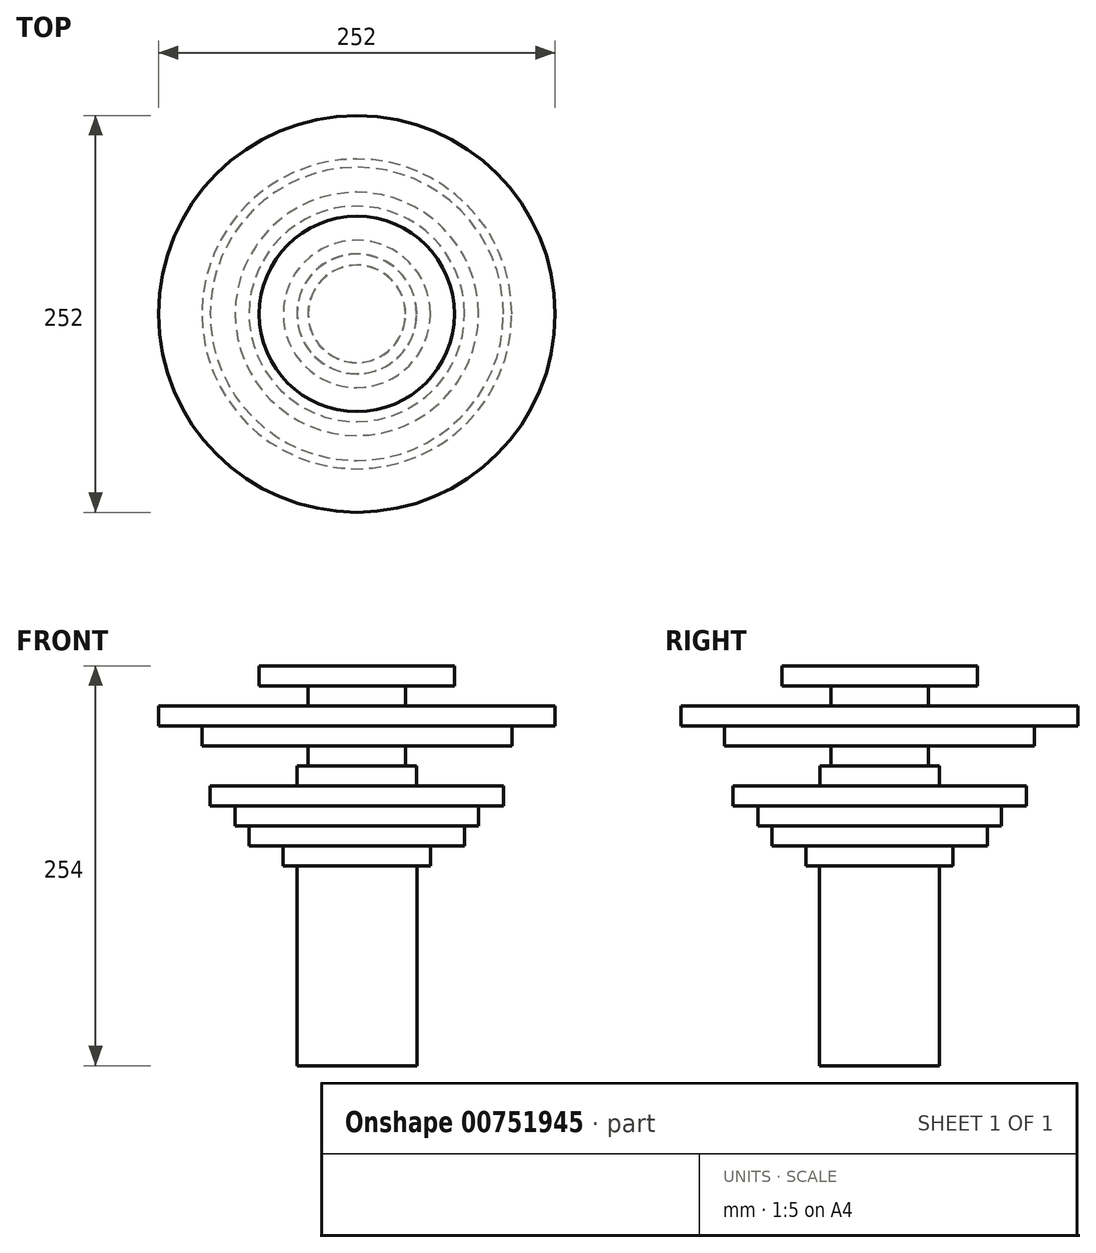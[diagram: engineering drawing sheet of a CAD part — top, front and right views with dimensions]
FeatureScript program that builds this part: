
annotation { "Feature Type Name" : "Feature", "Feature Type Description" : "" }
export const myFeature = defineFeature(function(context is Context, id is Id, definition is map)
    precondition{}
    {
        {
            var Q0;
            Q0=qCreatedBy(makeId("Front.planeOp"),FACE);
            var sketch = newSketch(context, id + "F0", { "sketchPlane" : qUnion([Q0])});
            skLineSegment(sketch, "E0.bottom", {"start": v(0, 10.4) * mm, "end": v(62, 10.4) * mm});
            skLineSegment(sketch, "E0.top", {"start": v(0, -2.3) * mm, "end": v(62, -2.3) * mm});
            skLineSegment(sketch, "E0.left", {"start": v(0, 10.4) * mm, "end": v(0, -2.3) * mm});
            skLineSegment(sketch, "E0.right", {"start": v(62, 10.4) * mm, "end": v(62, -2.3) * mm});
            skPoint(sketch, "E1.oppositeSnap0", {"position": v(31, -2.3) * mm});
            skLineSegment(sketch, "E1.bottom", {"start": v(0, -2.3) * mm, "end": v(31, -2.3) * mm});
            skLineSegment(sketch, "E1.top", {"start": v(0, -15) * mm, "end": v(31, -15) * mm});
            skLineSegment(sketch, "E1.left", {"start": v(0, -2.3) * mm, "end": v(0, -15) * mm});
            skLineSegment(sketch, "E1.right", {"start": v(31, -2.3) * mm, "end": v(31, -15) * mm});
            skLineSegment(sketch, "E2.bottom", {"start": v(0, -15) * mm, "end": v(126, -15) * mm});
            skLineSegment(sketch, "E2.top", {"start": v(0, -27.7) * mm, "end": v(126, -27.7) * mm});
            skLineSegment(sketch, "E2.left", {"start": v(0, -15) * mm, "end": v(0, -27.7) * mm});
            skLineSegment(sketch, "E2.right", {"start": v(126, -15) * mm, "end": v(126, -27.7) * mm});
            skLineSegment(sketch, "E3.bottom", {"start": v(0, -27.7) * mm, "end": v(98.4, -27.7) * mm});
            skLineSegment(sketch, "E3.top", {"start": v(0, -40.4) * mm, "end": v(98.4, -40.4) * mm});
            skLineSegment(sketch, "E3.left", {"start": v(0, -27.7) * mm, "end": v(0, -40.4) * mm});
            skLineSegment(sketch, "E3.right", {"start": v(98.4, -27.7) * mm, "end": v(98.4, -40.4) * mm});
            skLineSegment(sketch, "E4.bottom", {"start": v(0, -40.4) * mm, "end": v(30.9, -40.4) * mm});
            skLineSegment(sketch, "E4.top", {"start": v(0, -53.1) * mm, "end": v(30.9, -53.1) * mm});
            skLineSegment(sketch, "E4.left", {"start": v(0, -40.4) * mm, "end": v(0, -53.1) * mm});
            skLineSegment(sketch, "E4.right", {"start": v(30.9, -40.4) * mm, "end": v(30.9, -53.1) * mm});
            skLineSegment(sketch, "E5.bottom", {"start": v(0, -53.1) * mm, "end": v(37.94, -53.1) * mm});
            skLineSegment(sketch, "E5.top", {"start": v(0, -65.8) * mm, "end": v(37.94, -65.8) * mm});
            skLineSegment(sketch, "E5.left", {"start": v(0, -53.1) * mm, "end": v(0, -65.8) * mm});
            skLineSegment(sketch, "E5.right", {"start": v(37.94, -53.1) * mm, "end": v(37.94, -65.8) * mm});
            skLineSegment(sketch, "E6.bottom", {"start": v(0, -65.8) * mm, "end": v(93.12, -65.8) * mm});
            skLineSegment(sketch, "E6.top", {"start": v(0, -78.5) * mm, "end": v(93.12, -78.5) * mm});
            skLineSegment(sketch, "E6.left", {"start": v(0, -65.8) * mm, "end": v(0, -78.5) * mm});
            skLineSegment(sketch, "E6.right", {"start": v(93.12, -65.8) * mm, "end": v(93.12, -78.5) * mm});
            skLineSegment(sketch, "E7.bottom", {"start": v(0, -78.5) * mm, "end": v(77.27, -78.5) * mm});
            skLineSegment(sketch, "E7.top", {"start": v(0, -91.2) * mm, "end": v(77.27, -91.2) * mm});
            skLineSegment(sketch, "E7.left", {"start": v(0, -78.5) * mm, "end": v(0, -91.2) * mm});
            skLineSegment(sketch, "E7.right", {"start": v(77.27, -78.5) * mm, "end": v(77.27, -91.2) * mm});
            skLineSegment(sketch, "E8.bottom", {"start": v(0, -91.2) * mm, "end": v(68.47, -91.2) * mm});
            skLineSegment(sketch, "E8.top", {"start": v(0, -103.9) * mm, "end": v(68.47, -103.9) * mm});
            skLineSegment(sketch, "E8.left", {"start": v(0, -91.2) * mm, "end": v(0, -103.9) * mm});
            skLineSegment(sketch, "E8.right", {"start": v(68.47, -91.2) * mm, "end": v(68.47, -103.9) * mm});
            skLineSegment(sketch, "E9.bottom", {"start": v(0, -103.9) * mm, "end": v(46.75, -103.9) * mm});
            skLineSegment(sketch, "E9.top", {"start": v(0, -116.6) * mm, "end": v(46.75, -116.6) * mm});
            skLineSegment(sketch, "E9.left", {"start": v(0, -103.9) * mm, "end": v(0, -116.6) * mm});
            skLineSegment(sketch, "E9.right", {"start": v(46.75, -103.9) * mm, "end": v(46.75, -116.6) * mm});
            skLineSegment(sketch, "E10.bottom", {"start": v(0, -116.6) * mm, "end": v(38.1, -116.6) * mm});
            skLineSegment(sketch, "E10.top", {"start": v(0, -243.6) * mm, "end": v(38.1, -243.6) * mm});
            skLineSegment(sketch, "E10.left", {"start": v(0, -116.6) * mm, "end": v(0, -243.6) * mm});
            skLineSegment(sketch, "E10.right", {"start": v(38.1, -116.6) * mm, "end": v(38.1, -243.6) * mm});
            skSolve(sketch);
        }
        {
            var Q0;
            Q0 = qSketchRegion(id + "F0", true);
            var Q1;
            Q1=sQuery(id+"F0.wireOp",EDGE,"E10.left");
            var Q2;
            Q2=sQuery(id+"F0.wireOp",EDGE,"E9.left");
            var Q3;
            Q3=sQuery(id+"F0.wireOp",EDGE,"E8.left");
            var Q4;
            Q4=sQuery(id+"F0.wireOp",EDGE,"E7.left");
            var Q5;
            Q5=sQuery(id+"F0.wireOp",EDGE,"E5.left");
            var Q6;
            Q6=sQuery(id+"F0.wireOp",EDGE,"E6.left");
            var Q7;
            Q7=sQuery(id+"F0.wireOp",EDGE,"E4.left");
            var Q8;
            Q8=sQuery(id+"F0.wireOp",EDGE,"E3.left");
            var Q9;
            Q9=sQuery(id+"F0.wireOp",EDGE,"E2.left");
            var Q10;
            Q10=sQuery(id+"F0.wireOp",EDGE,"E1.left");
            var Q11;
            Q11=sQuery(id+"F0.wireOp",EDGE,"E0.left");
            var Q12;
            Q12=sQuery(id+"F0.wireOp",EDGE,"E10.left");
            revolve(context, id + "F1", {"surfaceOperationType" : NewSurfaceOperationType.NEW, "entities" : qUnion([Q0]), "surfaceEntities" : qUnion([Q1, Q2, Q3, Q4, Q5, Q6, Q7, Q8, Q9, Q10, Q11]), "axis" : qUnion([Q12]), "revolveType" : RevolveType.FULL});
        }
    });
